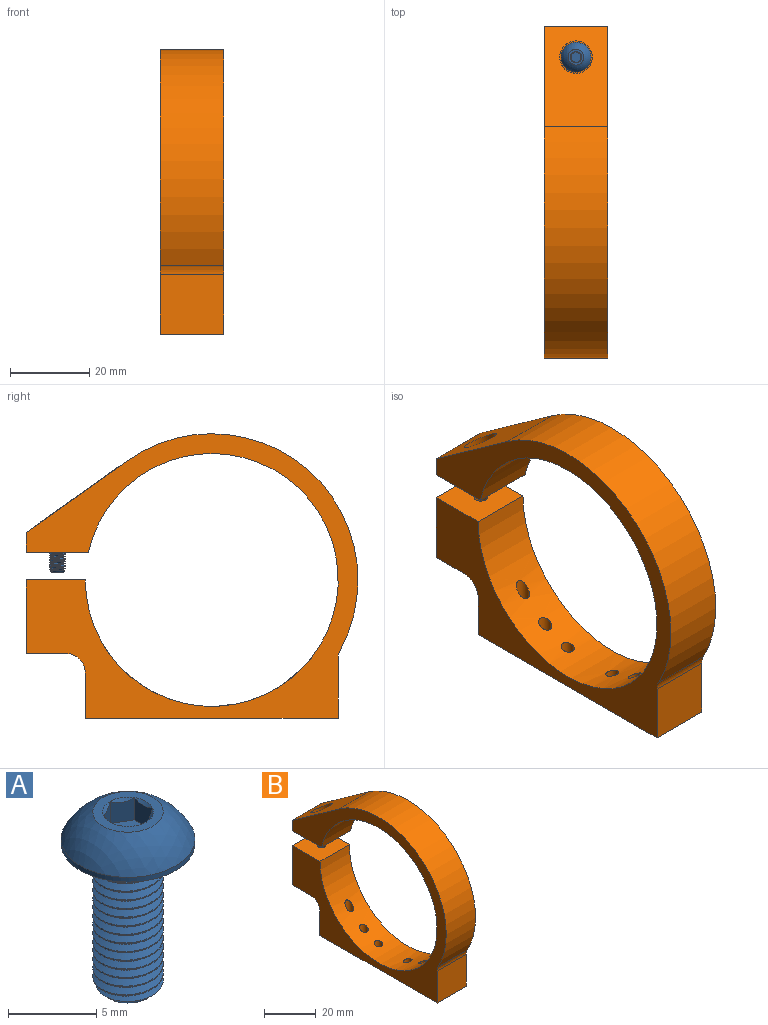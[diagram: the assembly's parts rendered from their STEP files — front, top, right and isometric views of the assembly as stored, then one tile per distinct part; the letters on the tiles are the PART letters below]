
ASSEMBLY  parts=2 mates=1
PART A: 23 faces, bbox 8.2x8.2x13.4 mm
  f0: cone r=1.44mm half-angle=45deg, axis (0,0,1), area 0.2mm2, adj f9,f17
  f1: cylinder r=3.8mm len=7.6mm, axis (0,0,1), area 7.9mm2, adj f2,f10
  f2: sphere r=4.23mm, area 49.7mm2, adj f1,f9
  f3: cone r=1.55mm half-angle=45deg, axis (0,0,1), area 3.9mm2, adj f4,f5,f6,f7,f8
  f4: cylinder r=2mm len=9.55mm, axis (0,0,-1), area 15mm2, adj f3,f6,f8,f10
  f5: plane 3.1x3.1mm, normal (0,0,-1), area 7.5mm2, adj f3
  f6: bspline ~10.39x4mm, area 82.9mm2, adj f3,f4,f7,f10
  f7: cylinder r=1.61mm len=9.94mm, axis (0,0,-1), area 1.9mm2, adj f3,f6,f8,f10
  f8: bspline ~10.16x4mm, area 82.5mm2, adj f3,f4,f7,f10
  f9: plane 4.47x4.47mm, normal (0,0,1), area 6mm2, adj f0,f2,f11,f12,f13,f14,f15
  f10: plane 7.84x7.84mm, normal (0,0,-1), area 35.1mm2, adj f1,f4,f6,f7,f8
  f11: cone r=1.44mm half-angle=45deg, axis (0,0,1), area 0mm2, adj f9,f18
  f12: cone r=1.44mm half-angle=45deg, axis (0,0,1), area 0mm2, adj f9,f19
  f13: cone r=1.44mm half-angle=45deg, axis (0,0,1), area 0mm2, adj f9,f20
  f14: cone r=1.44mm half-angle=45deg, axis (0,0,1), area 0mm2, adj f9,f21
  f15: cone r=1.44mm half-angle=45deg, axis (0,0,1), area 0mm2, adj f9,f22
  f16: plane 2.89x2.5mm, normal (0,0,1), area 5.4mm2, adj f17,f18,f19,f20,f21,f22
  f17: plane 1.68x1.58mm, normal (-1,0,0), area 2mm2, adj f0,f16,f18,f22
  f18: plane 2.09x1.8mm, normal (-0.5,-0.87,0), area 2mm2, adj f11,f16,f17,f19
  f19: plane 2.09x1.8mm, normal (0.5,-0.87,0), area 2mm2, adj f12,f16,f18,f20
  f20: plane 2.09x1.99mm, normal (1,0,0), area 2mm2, adj f13,f16,f19,f21
  f21: plane 2.09x1.8mm, normal (0.5,0.87,0), area 2mm2, adj f14,f16,f20,f22
  f22: plane 2.09x1.8mm, normal (-0.5,0.87,0), area 2mm2, adj f15,f16,f17,f21
PART B: 25 faces, bbox 17.2x85.2x73.2 mm
  f0: cylinder r=32mm len=64.01mm, axis (-1,0,0), area 3041.4mm2, adj f1,f10,f11,f12,f13,f14,f15,f16
  f1: plane 16x15mm, normal (0,0,1), area 231.5mm2, adj f0,f2,f11,f12,f24
  f2: plane 18.58x16mm, normal (0,1,0), area 297.3mm2, adj f1,f3,f11,f12
  f3: plane 16x10mm, normal (0,0,-1), area 151.5mm2, adj f2,f11,f12,f19,f24
  f4: plane 16x11.42mm, normal (0,1,0), area 182.7mm2, adj f5,f11,f12,f19
  f5: plane 64x16mm, normal (0,0,-1), area 972.7mm2, adj f4,f6,f11,f12,f13,f14,f15,f16
  f6: plane 16x15.12mm, normal (0,-1,0), area 241.9mm2, adj f5,f11,f12,f20
  f7: cylinder r=37mm len=58.43mm, axis (-1,0,0), area 1587.6mm2, adj f8,f11,f12,f20
  f8: plane 26.81x19.4mm, normal (0,0.58,0.82), area 436.4mm2, adj f7,f9,f11,f12,f21
  f9: plane 16x5mm, normal (0,1,0), area 80mm2, adj f8,f10,f11,f12
  f10: plane 16x15.78mm, normal (0,0,-1), area 236.5mm2, adj f0,f9,f11,f12,f22
  f11: plane 84.01x72mm, normal (1,0,0), area 1623.4mm2, adj f0,f1,f2,f3,f4,f5,f6,f7
  f12: plane 84.01x72mm, normal (-1,0,0), area 1623.4mm2, adj f0,f1,f2,f3,f4,f5,f6,f7
  f13: cylinder r=1.65mm len=15.86mm, axis (0,0,-1), area 144.1mm2, adj f0,f5
  f14: cylinder r=1.65mm len=8.3mm, axis (0,0,-1), area 75.8mm2, adj f0,f5
  f15: cylinder r=1.65mm len=4.01mm, axis (0,0,-1), area 41.6mm2, adj f0,f5
  f16: cylinder r=1.65mm len=4.01mm, axis (0,0,-1), area 41.6mm2, adj f0,f5
  f17: cylinder r=1.65mm len=8.3mm, axis (0,0,-1), area 75.8mm2, adj f0,f5
  f18: cylinder r=1.65mm len=15.86mm, axis (0,0,-1), area 144.1mm2, adj f0,f5
  f19: cylinder r=5mm len=16mm, axis (1,0,0), area 125.7mm2, adj f3,f4,f11,f12
  f20: cylinder r=5mm len=16mm, axis (-1,0,0), area 39.4mm2, adj f6,f7,f11,f12
  f21: cylinder r=4.12mm len=8.53mm, axis (0,0,1), area 142.6mm2, adj f8,f23
  f22: cylinder r=2.25mm len=5mm, axis (0,0,1), area 70.7mm2, adj f10,f23
  f23: plane 8.25x8.25mm, normal (0,0,1), area 37.6mm2, adj f21,f22
  f24: cylinder r=1.65mm len=18.58mm, axis (0,0,1), area 192.6mm2, adj f1,f3
PLACE A t=(19.52,18.1,6.03)mm
PLACE B t=(30.36,-27.73,10.15)mm
MATE fastened B.f24 <-> A.f0  axis (0,0,1) through (19.52,18.1,3.83)mm
